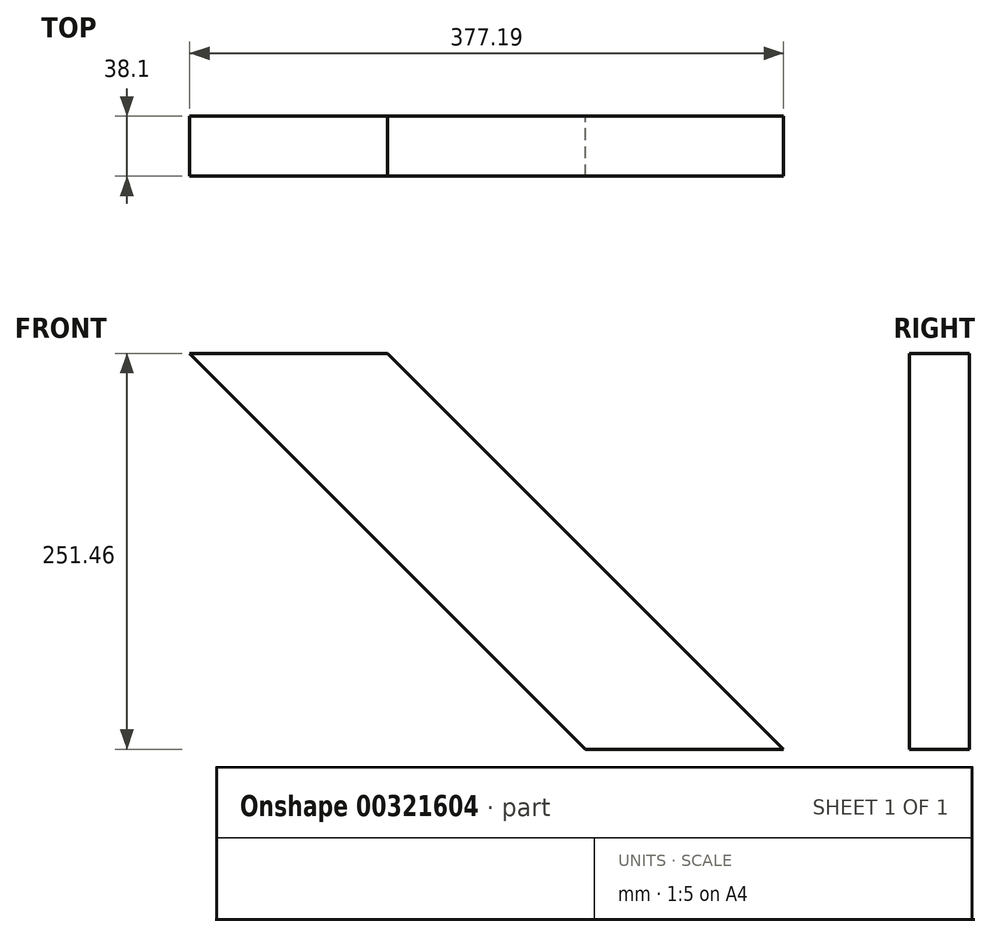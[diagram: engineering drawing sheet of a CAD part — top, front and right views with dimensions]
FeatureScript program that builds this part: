
annotation { "Feature Type Name" : "Feature", "Feature Type Description" : "" }
export const myFeature = defineFeature(function(context is Context, id is Id, definition is map)
    precondition{}
    {
        {
            var Q0;
            Q0=qCreatedBy(makeId("Front.planeOp"),FACE);
            var sketch = newSketch(context, id + "F0", { "sketchPlane" : qUnion([Q0])});
            skLineSegment(sketch, "E0", {"start": v(0, 251.46) * mm, "end": v(125.73, 251.46) * mm});
            skLineSegment(sketch, "E1", {"start": v(125.73, 251.46) * mm, "end": v(377.2, 0) * mm});
            skLineSegment(sketch, "E2", {"start": v(377.2, 0) * mm, "end": v(251.46, 0) * mm});
            skLineSegment(sketch, "E3", {"start": v(251.46, 0) * mm, "end": v(0, 251.46) * mm});
            skSolve(sketch);
        }
        {
            var Q0;
            Q0=makeQuery(id+"F0.imprint","IMPRINT",FACE,{"disambiguationData":[TD([[makeQuery(id+"F0.imprint","IMPRINT",EDGE,{"derivedFrom":sQuery(id+"F0.wireOp",EDGE,"E0")}),-1.0]])]});
            extrude(context, id + "F1", {"entities" : qUnion([Q0]), "depth" : 38.1 * mm});
        }
    });
